# Revit family: Bitpop 8.1
name_source: partatom
category: Lighting Fixtures
revit_build: Autodesk Revit 2017 (Build: 20160225_1515(x64)
units: mm (PartAtom-declared; Revit-internal decimal feet)

## family parameters
Cut with Voids When Loaded = Yes
Host = Face
Light Source = Yes
Part Type = Normal
Room Calculation Point = Yes
Round Connector Dimension = Use Diameter
Shared = No

## types (8) — shared parameters
Apparent Load Phase 1 = 50 W
Body = L&L_Black anodized aluminium
CRI = 90 (also available: CRI 80 - ref. URL Technical sheet)
Code = BP8110 B White; BP8110 N Black; BP8111 B White; BP8111 N Black
Color Filter = 16777215
Control system = on/off; 1-10V + PUSH; DALI + PUSH
Cutout dimensions = 320x42 mm
Default Elevation = 1219 mm
Delivered lumen output = 1984 lm (3000K, 30°, 35W); 2680 lm (3000K, 30°, 50W)
Description = Indoor recessed
Dimming Lamp Color Temperature Shift = <None>
Emit from Line Length = 610 mm
Energy efficiency class = A A+ A++
Features = UGR < 10 for 17° and 30° optics
Height mm = 71 mm  [stored 0.23294 ft]
Height void = 42 mm  [stored 0.137795 ft]
IP = 40; 44 installed
LED Colour = 3000K (also available: 2700K and 4000K - ref. URL Technical sheet)
Length mm = 329 mm  [stored 1.0794 ft]
Lens = L&L_Lens
Lumen output at source = 2800 lm (3000K, 35W); 3840 lm (3000K, 50W)
Manufacturer = L&L Luce&Light
Material = body in black anodized aluminium trim in steel
Mounting = recessed (ceiling: flush or deep set)
No. and type of led = 8 high-intensity power LEDs
Notes = ceiling-mounted version Bitpop C
Power = 50W (also available: 35W - ref. URL Technical sheet)
Power cables = includes 0.30 m cable
Power supply = 230Vac
Power supply unit = included and wired
Tilt Angle = 90.00°
Trim = L&L_Steel
URL = https://www.lucelight.it
URL Accessories and power supply units = https://www.lucelight.it
URL Catalogue = https://www.lucelight.it
URL DXF = https://www.lucelight.it
URL Description = https://www.lucelight.it
URL General code = https://www.lucelight.it
URL IES Photometric file = https://www.lucelight.it
URL Image = https://www.lucelight.it
URL Technical sheet = https://www.lucelight.it
Voltage = 230 V
Weight kg = 1.10
Width mm = 49 mm  [stored 0.160761 ft]
Wiring = -

## per-type parameters (varying)
| type | Geometry | Length void | Model | Optics | Photometric Web File | Width void |
| Bitpop 8.1_ F 30° (3000K 50W 230Vac) | Bitpop8.1_mod : Bitpop 8.1 | 320 mm  [stored 1.04987 ft] | Bitpop 8.1 | 30° | BITPOP 8.1 F 30° [3000K 50W 230Vac].IES | 42 mm  [stored 0.137795 ft] |
| Bitpop 8.1_ L 42° (3000K 50W 230Vac) | Bitpop8.1_mod : Bitpop 8.1 | 320 mm  [stored 1.04987 ft] | Bitpop 8.1 | 42° | BITPOP 8.1 L 42° [3000K 50W 230Vac].IES | 42 mm  [stored 0.137795 ft] |
| Bitpop 8.1_ S 17° (3000K 50W 230Vac) | Bitpop8.1_mod : Bitpop 8.1 | 320 mm  [stored 1.04987 ft] | Bitpop 8.1 | 17° | BITPOP 8.1 S 17° [3000K 50W 230Vac].IES | 42 mm  [stored 0.137795 ft] |
| Bitpop 8.1_ W 17°x45° (3000K 50W 230Vac) | Bitpop8.1_mod : Bitpop 8.1 | 320 mm  [stored 1.04987 ft] | Bitpop 8.1 | 17°x45° | BITPOP 8.1 W 17°x45° [3000K 50W 230Vac].IES | 42 mm  [stored 0.137795 ft] |
| Bitpop 8.1_Recessed_ F 30° (3000K 50W 230Vac) | Bitpop8.1_Recessed_mod : Bitpop 8.1 recessed | 333 mm  [stored 1.09252 ft] | Bitpop 8.1_Recessed | 30° | BITPOP 8.1 F 30° [3000K 50W 230Vac].IES | 53 mm  [stored 0.173885 ft] |
| Bitpop 8.1_Recessed_ L 42° (3000K 50W 230Vac) | Bitpop8.1_Recessed_mod : Bitpop 8.1 recessed | 333 mm  [stored 1.09252 ft] | Bitpop 8.1_Recessed | 42° | BITPOP 8.1 L 42° [3000K 50W 230Vac].IES | 53 mm  [stored 0.173885 ft] |
| Bitpop 8.1_Recessed_ S 17° (3000K 50W 230Vac) | Bitpop8.1_Recessed_mod : Bitpop 8.1 recessed | 333 mm  [stored 1.09252 ft] | Bitpop 8.1_Recessed | 17° | BITPOP 8.1 S 17° [3000K 50W 230Vac].IES | 53 mm  [stored 0.173885 ft] |
| Bitpop 8.1_Recessed_ W 17°x45° (3000K 50W 230Vac) | Bitpop8.1_Recessed_mod : Bitpop 8.1 recessed | 333 mm  [stored 1.09252 ft] | Bitpop 8.1_Recessed | 17°x45° | BITPOP 8.1 W 17°x45° [3000K 50W 230Vac].IES | 53 mm  [stored 0.173885 ft] |

note: [stored X ft] marks values corroborated as IEEE doubles in the binary element streams (Revit-internal decimal feet)

## geometry (parser evidence)
native form markers: Blend x2, Sweep x8
no freeform markers — native parametric forms only
